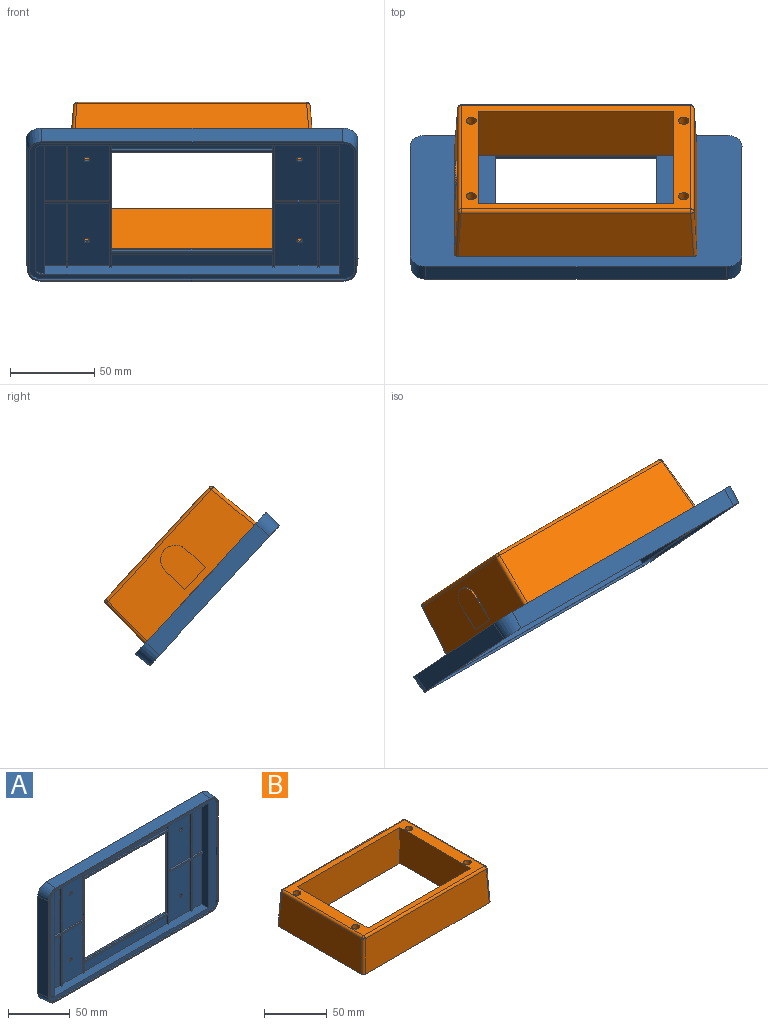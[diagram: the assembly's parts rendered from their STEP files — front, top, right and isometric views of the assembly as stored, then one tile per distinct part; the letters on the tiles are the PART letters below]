
ASSEMBLY  parts=2 mates=1
PART A: 77 faces, bbox 196.9x11x114.9 mm
  f0: plane 95.57x9.86mm, normal (0,-1,0), area 942mm2, adj f1,f2,f18,f76
  f1: plane 9.86x1.5mm, normal (1,0,0), area 14.8mm2, adj f0,f18,f58,f76
  f2: plane 9.86x1.5mm, normal (-1,0,0), area 14.8mm2, adj f0,f18,f58,f76
  f3: plane 95.57x81.22mm, normal (0,-1,0), area 66.6mm2, adj f4,f5,f47,f48,f49,f50,f74,f75
  f4: plane 81.22x1.5mm, normal (1,0,0), area 121.8mm2, adj f3,f58,f74,f75
  f5: plane 81.22x1.5mm, normal (-1,0,0), area 121.8mm2, adj f3,f58,f74,f75
  f6: plane 51.25x25.47mm, normal (0,-1,0), area 1295.5mm2, adj f7,f8,f23,f53,f71
  f7: plane 51.25x1.5mm, normal (1,0,0), area 76.9mm2, adj f6,f23,f58,f71
  f8: plane 51.25x1.5mm, normal (-1,0,0), area 76.9mm2, adj f6,f23,f58,f71
  f9: plane 51.25x12.11mm, normal (0,-1,0), area 620.8mm2, adj f10,f11,f23,f69
  f10: plane 51.25x1.5mm, normal (1,0,0), area 76.9mm2, adj f9,f23,f58,f69
  f11: plane 104x7.9mm, normal (-1,0,0), area 819.4mm2, adj f9,f17,f18,f23,f42,f58,f69,f70
  f12: plane 51.25x24.99mm, normal (0,-1,0), area 1271.1mm2, adj f13,f14,f18,f55,f68
  f13: plane 51.25x1.5mm, normal (-1,0,0), area 76.9mm2, adj f12,f18,f58,f68
  f14: plane 51.25x1.5mm, normal (1,0,0), area 76.9mm2, adj f12,f18,f58,f68
  f15: plane 51.25x13.07mm, normal (0,-1,0), area 669.7mm2, adj f16,f18,f22,f66
  f16: plane 51.25x1.5mm, normal (-1,0,0), area 76.9mm2, adj f15,f18,f58,f66
  f17: plane 51.25x12.11mm, normal (0,-1,0), area 620.8mm2, adj f11,f18,f63,f70
  f18: plane 176.5x7.9mm, normal (0,0,-1), area 1379.4mm2, adj f0,f1,f2,f11,f12,f13,f14,f15
  f19: plane 51.25x25.47mm, normal (0,-1,0), area 1295.5mm2, adj f18,f54,f61,f64,f72
  f20: plane 51.25x24.99mm, normal (0,-1,0), area 1271.1mm2, adj f23,f52,f57,f59,f67
  f21: plane 95.57x9.92mm, normal (0,-1,0), area 948.5mm2, adj f23,f56,f62,f73
  f22: plane 104x6.9mm, normal (1,0,0), area 715.4mm2, adj f15,f18,f23,f46,f51,f58,f65,f66
  f23: plane 176.5x7.9mm, normal (0,0,1), area 1379.4mm2, adj f6,f7,f8,f9,f10,f11,f20,f21
  f24: plane 196.92x114.92mm, normal (0,1,0), area 14821.2mm2, adj f26,f27,f28,f29,f30,f31,f32,f33
  f25: plane 195x113mm, normal (0,-1,0), area 598.3mm2, adj f26,f27,f28,f29,f30,f31,f32,f33
  f26: plane 96x11mm, normal (1,-0.09,0), area 1060mm2, adj f24,f25,f27,f33
  f27: cone r=8.5mm half-angle=5deg, axis (0,1,0), area 155.8mm2, adj f24,f25,f26,f28
  f28: plane 178x11mm, normal (0,-0.09,1), area 1965.5mm2, adj f24,f25,f27,f29
  f29: cone r=8.5mm half-angle=5deg, axis (0,1,0), area 155.8mm2, adj f24,f25,f28,f30
  f30: plane 96x11mm, normal (-1,-0.09,0), area 1060mm2, adj f24,f25,f29,f31
  f31: cone r=8.5mm half-angle=5deg, axis (0,1,0), area 155.8mm2, adj f24,f25,f30,f32
  f32: plane 178x11mm, normal (0,-0.09,-1), area 1965.5mm2, adj f24,f25,f31,f33
  f33: cone r=8.5mm half-angle=5deg, axis (0,1,0), area 155.8mm2, adj f24,f25,f26,f32
  f34: plane 96x1.5mm, normal (-1,0,0), area 144mm2, adj f25,f35,f41,f42
  f35: cylinder r=7.5mm len=7.5mm, axis (0,-1,0), area 17.7mm2, adj f25,f34,f36,f42
  f36: plane 178x1.5mm, normal (0,0,-1), area 267mm2, adj f25,f35,f37,f42
  f37: cylinder r=7.5mm len=7.5mm, axis (0,-1,0), area 17.7mm2, adj f25,f36,f38,f42
  f38: plane 96x1.5mm, normal (1,0,0), area 144mm2, adj f25,f37,f39,f42
  f39: cylinder r=7.5mm len=7.5mm, axis (0,-1,0), area 17.7mm2, adj f25,f38,f40,f42
  f40: plane 178x1.5mm, normal (0,0,1), area 267mm2, adj f25,f39,f41,f42
  f41: cylinder r=7.5mm len=7.5mm, axis (0,-1,0), area 17.7mm2, adj f25,f34,f40,f42
  f42: plane 193x111mm, normal (0,-1,0), area 2609.6mm2, adj f11,f18,f23,f34,f35,f36,f37,f38
  f43: cylinder r=4mm len=4mm, axis (0,-1,0), area 6.3mm2, adj f23,f42,f45,f46
  f44: cylinder r=4mm len=4mm, axis (0,-1,0), area 6.3mm2, adj f18,f42,f45,f46
  f45: plane 96x1mm, normal (1,0,0), area 96mm2, adj f42,f43,f44,f46
  f46: plane 104x5.3mm, normal (0,-1,0), area 544.3mm2, adj f18,f22,f23,f43,f44,f45
  f47: plane 95x1.6mm, normal (0,0,1), area 152mm2, adj f3,f24,f48,f50
  f48: plane 81x1.6mm, normal (-1,0,0), area 129.6mm2, adj f3,f24,f47,f49
  f49: plane 95x1.6mm, normal (0,0,-1), area 152mm2, adj f3,f24,f48,f50
  f50: plane 81x1.6mm, normal (1,0,0), area 129.6mm2, adj f3,f24,f47,f49
  f51: plane 51.25x13.07mm, normal (0,-1,0), area 669.7mm2, adj f22,f23,f60,f65
  f52: cylinder r=1.75mm len=3.5mm, axis (0,1,0), area 17.6mm2, adj f20,f24
  f53: cylinder r=1.75mm len=3.5mm, axis (0,1,0), area 17.6mm2, adj f6,f24
  f54: cylinder r=1.75mm len=3.5mm, axis (0,1,0), area 17.6mm2, adj f19,f24
  f55: cylinder r=1.75mm len=3.5mm, axis (0,1,0), area 17.6mm2, adj f12,f24
  f56: plane 9.92x1.5mm, normal (1,0,0), area 14.9mm2, adj f21,f23,f58,f73
  f57: plane 51.25x1.5mm, normal (-1,0,0), area 76.9mm2, adj f20,f23,f58,f67
  f58: plane 175.2x104mm, normal (0,-1,0), area 816.1mm2, adj f1,f2,f4,f5,f7,f8,f10,f11
  f59: plane 51.25x1.5mm, normal (1,0,0), area 76.9mm2, adj f20,f23,f58,f67
  f60: plane 51.25x1.5mm, normal (-1,0,0), area 76.9mm2, adj f23,f51,f58,f65
  f61: plane 51.25x1.5mm, normal (1,0,0), area 76.9mm2, adj f18,f19,f58,f72
  f62: plane 9.92x1.5mm, normal (-1,0,0), area 14.9mm2, adj f21,f23,f58,f73
  f63: plane 51.25x1.5mm, normal (1,0,0), area 76.9mm2, adj f17,f18,f58,f70
  f64: plane 51.25x1.5mm, normal (-1,0,0), area 76.9mm2, adj f18,f19,f58,f72
  f65: plane 13.07x1.5mm, normal (0,0,-1), area 19.6mm2, adj f22,f51,f58,f60
  f66: plane 13.07x1.5mm, normal (0,0,1), area 19.6mm2, adj f15,f16,f22,f58
  f67: plane 24.99x1.5mm, normal (0,0,-1), area 37.5mm2, adj f20,f57,f58,f59
  f68: plane 24.99x1.5mm, normal (0,0,1), area 37.5mm2, adj f12,f13,f14,f58
  f69: plane 12.11x1.5mm, normal (0,0,-1), area 18.2mm2, adj f9,f10,f11,f58
  f70: plane 12.11x1.5mm, normal (0,0,1), area 18.2mm2, adj f11,f17,f58,f63
  f71: plane 25.47x1.5mm, normal (0,0,-1), area 38.2mm2, adj f6,f7,f8,f58
  f72: plane 25.47x1.5mm, normal (0,0,1), area 38.2mm2, adj f19,f58,f61,f64
  f73: plane 95.57x1.5mm, normal (0,0,-1), area 143.3mm2, adj f21,f56,f58,f62
  f74: plane 95.57x1.5mm, normal (0,0,1), area 143.3mm2, adj f3,f4,f5,f58
  f75: plane 95.57x1.5mm, normal (0,0,-1), area 143.3mm2, adj f3,f4,f5,f58
  f76: plane 95.57x1.5mm, normal (0,0,1), area 143.3mm2, adj f0,f1,f2,f58
PART B: 38 faces, bbox 143.7x97.7x35 mm
  f0: plane 139.67x33.1mm, normal (0,1,0.05), area 4572.7mm2, adj f8,f24,f30,f33
  f1: plane 93.67x33.1mm, normal (-1,0,0.05), area 3047.8mm2, adj f8,f27,f31,f33
  f2: plane 139.67x33.1mm, normal (0,-1,0.05), area 4572.7mm2, adj f8,f22,f26,f27
  f3: plane 80x35mm, normal (1,0,0), area 2800mm2, adj f4,f6,f8,f9
  f4: plane 116x35mm, normal (0,-1,0), area 4060mm2, adj f3,f5,f8,f9
  f5: plane 80x35mm, normal (-1,0,0), area 2800mm2, adj f4,f6,f8,f9
  f6: plane 116x35mm, normal (0,1,0), area 4060mm2, adj f3,f5,f8,f9
  f7: plane 93.67x33.1mm, normal (1,0,0.05), area 2643.1mm2, adj f8,f22,f24,f25,f34,f35,f36,f37
  f8: plane 143.67x97.67mm, normal (0,0,-1), area 4698.2mm2, adj f0,f1,f2,f3,f4,f5,f6,f7
  f9: plane 136.2x90.2mm, normal (0,0,1), area 2893.1mm2, adj f3,f4,f5,f6,f12,f15,f18,f21
  f10: cylinder r=2mm len=13mm, axis (0,0,1), area 163.4mm2, adj f8,f11
  f11: plane 6x6mm, normal (0,0,1), area 15.7mm2, adj f10,f12
  f12: cylinder r=3mm len=22mm, axis (0,0,1), area 414.7mm2, adj f9,f11
  f13: cylinder r=2mm len=13mm, axis (0,0,1), area 163.4mm2, adj f8,f14
  f14: plane 6x6mm, normal (0,0,1), area 15.7mm2, adj f13,f15
  f15: cylinder r=3mm len=22mm, axis (0,0,1), area 414.7mm2, adj f9,f14
  f16: cylinder r=2mm len=13mm, axis (0,0,1), area 163.4mm2, adj f8,f17
  f17: plane 6x6mm, normal (0,0,1), area 15.7mm2, adj f16,f18
  f18: cylinder r=3mm len=22mm, axis (0,0,1), area 414.7mm2, adj f9,f17
  f19: cylinder r=2mm len=13mm, axis (0,0,1), area 163.4mm2, adj f8,f20
  f20: plane 6x6mm, normal (0,0,1), area 15.7mm2, adj f19,f21
  f21: cylinder r=3mm len=22mm, axis (0,0,1), area 414.7mm2, adj f9,f20
  f22: cylinder r=2mm len=33.19mm, axis (-0.05,0.05,1), area 104.2mm2, adj f2,f7,f8,f23
  f23: sphere r=2mm, area 5.9mm2, adj f22,f25,f26
  f24: cylinder r=2mm len=33.19mm, axis (-0.05,-0.05,1), area 104.2mm2, adj f0,f7,f8,f28
  f25: cylinder r=2mm len=90.2mm, axis (0,-1,0), area 273.9mm2, adj f7,f9,f23,f28
  f26: cylinder r=2mm len=136.2mm, axis (1,0,0), area 413.6mm2, adj f2,f9,f23,f29
  f27: cylinder r=2mm len=33.19mm, axis (0.05,0.05,1), area 104.2mm2, adj f1,f2,f8,f29
  f28: sphere r=2mm, area 5.9mm2, adj f24,f25,f30
  f29: sphere r=2mm, area 5.9mm2, adj f26,f27,f31
  f30: cylinder r=2mm len=136.2mm, axis (1,0,0), area 413.6mm2, adj f0,f9,f28,f32
  f31: cylinder r=2mm len=90.2mm, axis (0,-1,0), area 273.9mm2, adj f1,f9,f29,f32
  f32: sphere r=2mm, area 5.9mm2, adj f30,f31,f33
  f33: cylinder r=2mm len=33.19mm, axis (0.05,-0.05,1), area 104.2mm2, adj f0,f1,f8,f32
  f34: cylinder r=8.89mm len=17.78mm, axis (-1,0,0), area 31.3mm2, adj f7,f35,f36,f37
  f35: plane 15.75x0.83mm, normal (0,1,0), area 6.5mm2, adj f7,f34,f37
  f36: plane 15.75x0.83mm, normal (0,-1,0), area 6.5mm2, adj f7,f34,f37
  f37: plane 24.64x17.78mm, normal (1,0,0), area 404.2mm2, adj f7,f34,f35,f36
PLACE A rot(axis=(1,0,0),42.8deg) t=(82.11,94.75,-32.29)mm
PLACE B rot(axis=(0,0.4,0.92),180deg) t=(82.01,120.55,-8.64)mm
MATE revolute B.f19 <-> A.f53  axis (0,-0.73,-0.68) through (146.01,116.59,-55.9)mm
